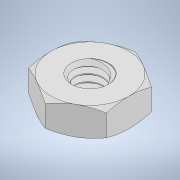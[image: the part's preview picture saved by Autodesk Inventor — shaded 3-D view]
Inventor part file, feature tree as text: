
AUTODESK INVENTOR PART (.ipt)
format: ipt  version: 2021 (Build 250183000, 183)  size: 226,304 bytes
history: mixed  units: in
note: dims shown in document units (in); Inventor stores cm internally (conversion verified against a paired STEP export)
features: mirror x1, imported_body x1
ambient origin geometry x8: Origin, YZ Plane, XZ Plane, XY Plane, X Axis, Y Axis, Z Axis, Center Point
bodies: Solid1 (imported_parasolid)
feature tree (2):
  mirror  "Mirror1"
  imported_body  NMx_Import_Brep_tag  [imported B-rep: ~2 faces, bbox_mm=None]
